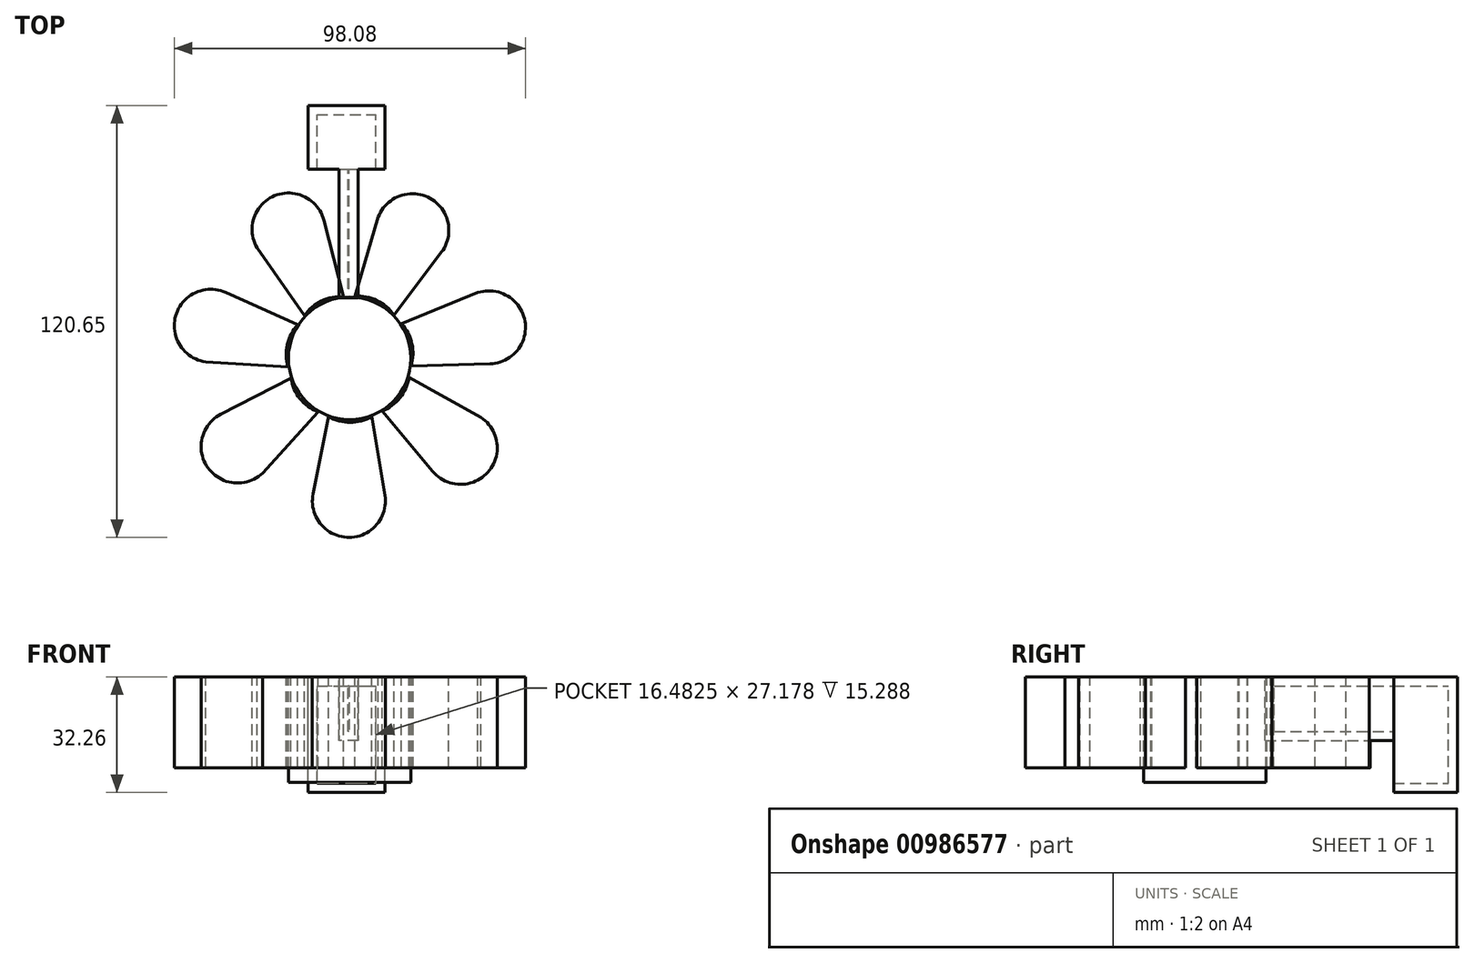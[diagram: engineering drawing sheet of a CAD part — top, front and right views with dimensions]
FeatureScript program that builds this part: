
annotation { "Feature Type Name" : "Feature", "Feature Type Description" : "" }
export const myFeature = defineFeature(function(context is Context, id is Id, definition is map)
    precondition{}
    {
        {
            var Q0;
            Q0=qCreatedBy(makeId("Top.planeOp"),FACE);
            var sketch = newSketch(context, id + "F0", { "sketchPlane" : qUnion([Q0])});
            skCircle(sketch, "E0", {"center": v(0, 0) * mm, "radius": 17.1 * mm});
            skSolve(sketch);
        }
        {
            var Q0;
            Q0=qCreatedBy(makeId("Top.planeOp"),FACE);
            var sketch = newSketch(context, id + "F1", { "sketchPlane" : qUnion([Q0])});
            skLineSegment(sketch, "E1", {"start": v(-5.9, -16.26) * mm, "end": v(-10.22, -37.85) * mm});
            skLineSegment(sketch, "E2", {"start": v(6.19, -16.26) * mm, "end": v(9.93, -39) * mm});
            skArc(sketch, "E3", {"start": v(-10.22, -37.85) * mm, "mid": v(-0.8, -50.02) * mm, "end": v(9.93, -39) * mm});
            skArc(sketch, "E4", {"start": v(-5.9, -16.26) * mm, "mid": v(0.14, -17.87) * mm, "end": v(6.19, -16.26) * mm});
            skArc(sketch, "E5.1.0", {"start": v(9.03, -14.75) * mm, "mid": v(14.06, -11.03) * mm, "end": v(16.57, -5.3) * mm});
            skLineSegment(sketch, "E5.1.1", {"start": v(16.57, -5.3) * mm, "end": v(36.68, -16.55) * mm});
            skLineSegment(sketch, "E5.1.2", {"start": v(9.03, -14.75) * mm, "end": v(23.22, -31.58) * mm});
            skArc(sketch, "E5.2.0", {"start": v(17.17, -2.13) * mm, "mid": v(17.39, 4.12) * mm, "end": v(14.48, 9.65) * mm});
            skLineSegment(sketch, "E5.2.1", {"start": v(14.48, 9.65) * mm, "end": v(35.81, 18.36) * mm});
            skLineSegment(sketch, "E5.2.2", {"start": v(17.17, -2.13) * mm, "end": v(39.17, -1.54) * mm});
            skPoint(sketch, "E5.center", {"position": v(0, 0) * mm});
            skArc(sketch, "E6.2.3.0", {"start": v(12.37, 12.1) * mm, "mid": v(7.62, 16.16) * mm, "end": v(1.48, 17.34) * mm});
            skLineSegment(sketch, "E6.4.3.0", {"start": v(1.48, 17.34) * mm, "end": v(7.97, 39.44) * mm});
            skLineSegment(sketch, "E6.7.3.0", {"start": v(12.37, 12.1) * mm, "end": v(25.63, 29.67) * mm});
            skArc(sketch, "E6.2.4.0", {"start": v(-1.74, 17.21) * mm, "mid": v(-7.88, 16.04) * mm, "end": v(-12.63, 11.97) * mm});
            skLineSegment(sketch, "E6.4.4.0", {"start": v(-12.63, 11.97) * mm, "end": v(-25.87, 30.83) * mm});
            skLineSegment(sketch, "E6.7.4.0", {"start": v(-1.74, 17.21) * mm, "end": v(-7.22, 38.53) * mm});
            skArc(sketch, "E6.2.5.0", {"start": v(-14.54, 9.37) * mm, "mid": v(-17.45, 3.84) * mm, "end": v(-17.23, -2.41) * mm});
            skLineSegment(sketch, "E6.4.5.0", {"start": v(-17.23, -2.41) * mm, "end": v(-40.23, -1) * mm});
            skLineSegment(sketch, "E6.7.5.0", {"start": v(-14.54, 9.37) * mm, "end": v(-34.62, 18.38) * mm});
            skArc(sketch, "E6.2.6.0", {"start": v(-16.4, -5.53) * mm, "mid": v(-13.88, -11.25) * mm, "end": v(-8.86, -14.98) * mm});
            skLineSegment(sketch, "E6.4.6.0", {"start": v(-8.86, -14.98) * mm, "end": v(-24.3, -32.08) * mm});
            skLineSegment(sketch, "E6.7.6.0", {"start": v(-16.4, -5.53) * mm, "end": v(-35.96, -15.6) * mm});
            skArc(sketch, "E7.1.0", {"start": v(23.22, -31.58) * mm, "mid": v(38.6, -31.82) * mm, "end": v(36.68, -16.55) * mm});
            skArc(sketch, "E7.2.0", {"start": v(39.17, -1.54) * mm, "mid": v(48.94, 10.34) * mm, "end": v(35.81, 18.36) * mm});
            skArc(sketch, "E7.3.0", {"start": v(25.63, 29.67) * mm, "mid": v(22.43, 44.71) * mm, "end": v(7.97, 39.44) * mm});
            skArc(sketch, "E7.4.0", {"start": v(-7.22, 38.53) * mm, "mid": v(-20.98, 45.41) * mm, "end": v(-25.87, 30.83) * mm});
            skArc(sketch, "E7.5.0", {"start": v(-34.62, 18.38) * mm, "mid": v(-48.58, 11.92) * mm, "end": v(-40.23, -1) * mm});
            skArc(sketch, "E7.6.0", {"start": v(-35.96, -15.6) * mm, "mid": v(-39.6, -30.56) * mm, "end": v(-24.3, -32.08) * mm});
            skSolve(sketch);
        }
        {
            var Q0;
            Q0 = qSketchRegion(id + "F1", true);
            extrude(context, id + "F2", {"entities" : qUnion([Q0]), "oppositeDirection" : true, "depth" : 25.4 * mm, "offsetDistance" : 25.4 * mm});
        }
        {
            var Q0;
            Q0 = qSketchRegion(id + "F0", true);
            extrude(context, id + "F3", {"entities" : qUnion([Q0]), "oppositeDirection" : true, "depth" : 29.46 * mm, "offsetDistance" : 25.4 * mm});
        }
        {
            var Q0;
            Q0=qCreatedBy(makeId("Top.planeOp"),FACE);
            var sketch = newSketch(context, id + "F4", { "sketchPlane" : qUnion([Q0])});
            skLineSegment(sketch, "E8", {"start": v(-2.95, 16.88) * mm, "end": v(-2.95, 62.86) * mm});
            skLineSegment(sketch, "E9", {"start": v(2.38, 16.88) * mm, "end": v(2.38, 62.86) * mm});
            skLineSegment(sketch, "E10", {"start": v(2.38, 62.86) * mm, "end": v(-2.95, 62.86) * mm});
            skLineSegment(sketch, "E11", {"start": v(2.38, 16.88) * mm, "end": v(-2.95, 16.88) * mm});
            skSolve(sketch);
        }
        {
            var Q0;
            Q0=makeQuery(id+"F4.imprint","IMPRINT",FACE,{"disambiguationData":[TD([[makeQuery(id+"F4.imprint","IMPRINT",EDGE,{"derivedFrom":sQuery(id+"F4.wireOp",EDGE,"E8")}),-1.0]])]});
            extrude(context, id + "F5", {"entities" : qUnion([Q0]), "oppositeDirection" : true, "depth" : 17.78 * mm, "offsetDistance" : 25.4 * mm});
        }
        {
            var Q0;
            Q0=qCreatedBy(makeId("Top.planeOp"),FACE);
            var sketch = newSketch(context, id + "F6", { "sketchPlane" : qUnion([Q0])});
            skLineSegment(sketch, "E12.bottom", {"start": v(-11.67, 52.8) * mm, "end": v(9.9, 52.8) * mm});
            skLineSegment(sketch, "E12.top", {"start": v(-11.67, 70.62) * mm, "end": v(9.9, 70.62) * mm});
            skLineSegment(sketch, "E12.left", {"start": v(-11.67, 52.8) * mm, "end": v(-11.67, 70.62) * mm});
            skLineSegment(sketch, "E12.right", {"start": v(9.9, 52.8) * mm, "end": v(9.9, 70.62) * mm});
            skSolve(sketch);
        }
        {
            var Q0;
            Q0=makeQuery(id+"F6.imprint","IMPRINT",FACE,{"disambiguationData":[TD([[makeQuery(id+"F6.imprint","IMPRINT",EDGE,{"derivedFrom":sQuery(id+"F6.wireOp",EDGE,"E12.bottom")}),1.0]])]});
            extrude(context, id + "F7", {"entities" : qUnion([Q0]), "operationType" : NewBodyOperationType.ADD, "oppositeDirection" : true, "depth" : 32.26 * mm, "offsetDistance" : 25.4 * mm});
        }
        {
            var Q0;
            Q0=makeQuery(id+"F7.opExtrude","SWEPT_FACE",FACE,{"disambiguationData":[OSD([sQuery(id+"F6.wireOp",EDGE,"E12.bottom")])]});
            shell(context, id + "F8", {"entities" : qUnion([Q0]), "thickness" : 2.54 * mm});
        }
    });
